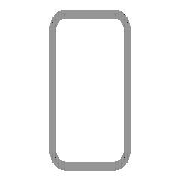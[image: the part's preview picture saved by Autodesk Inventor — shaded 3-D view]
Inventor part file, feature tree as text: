
AUTODESK INVENTOR PART (.ipt)
format: ipt  version: 2025 (Build 290162010, 162A)  size: 133,632 bytes
history: native  units: mm (DEFAULTED — no unit token found)
features: other x4, sketch x1, plane x1
ambient origin geometry x8: Origin, YZ Plane, XZ Plane, XY Plane, X Axis, Y Axis, Z Axis, Center Point
bodies: Solid1 (feature_tree), Body (feature_tree)
feature tree (6):
  parser-record x1  (decoder bookkeeping rows leaked as tree rows — omitted from the tree; the rows remain in map.json)
  other  "Driven Length"
  other  "Start Plane"
  other  "End Plane"
  sketch  "Sketch3"  dims[d3=841.0mm d4=0.0mm d7=6.0mm d9=40.0mm d11=60.0mm d12=3.0mm d13=-0.0mm d14=841.0mm d15=20.0mm d16=30.0mm d17=90.0deg d18=841.0mm]
  plane  "Work Plane3"
